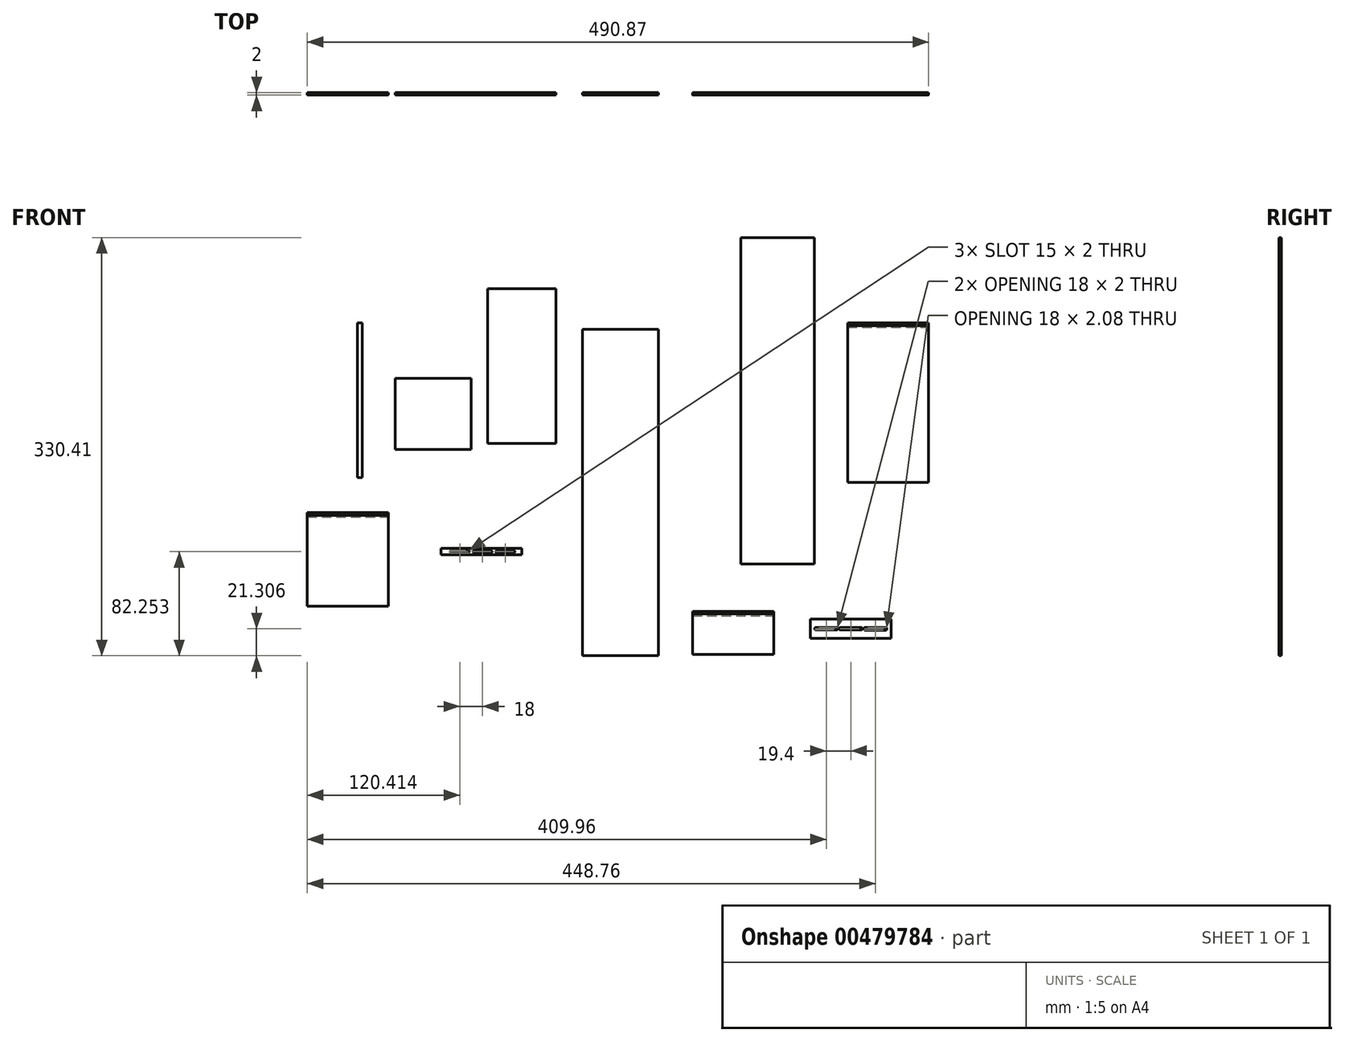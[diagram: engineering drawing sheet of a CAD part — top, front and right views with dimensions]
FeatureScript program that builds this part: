
annotation { "Feature Type Name" : "Feature", "Feature Type Description" : "" }
export const myFeature = defineFeature(function(context is Context, id is Id, definition is map)
    precondition{}
    {
        {
            var Q0;
            Q0=qCreatedBy(makeId("Front.planeOp"),FACE);
            var sketch = newSketch(context, id + "F0", { "sketchPlane" : qUnion([Q0])});
            skLineSegment(sketch, "E0.bottom", {"start": v(-75.81, 223.14) * mm, "end": v(-15.81, 223.14) * mm});
            skLineSegment(sketch, "E0.top", {"start": v(-75.81, -34.86) * mm, "end": v(-15.81, -34.86) * mm});
            skLineSegment(sketch, "E0.left", {"start": v(-75.81, 223.14) * mm, "end": v(-75.81, -34.86) * mm});
            skLineSegment(sketch, "E0.right", {"start": v(-15.81, 223.14) * mm, "end": v(-15.81, -34.86) * mm});
            skSolve(sketch);
        }
        {
            var Q0;
            Q0=makeQuery(id+"F0.imprint","IMPRINT",FACE,{"disambiguationData":[TD([[makeQuery(id+"F0.imprint","IMPRINT",EDGE,{"derivedFrom":sQuery(id+"F0.wireOp",EDGE,"E0.bottom")}),-1.0]])]});
            extrude(context, id + "F1", {"entities" : qUnion([Q0]), "depth" : 2 * mm});
        }
        {
            var Q0;
            Q0=qCreatedBy(makeId("Front.planeOp"),FACE);
            var sketch = newSketch(context, id + "F2", { "sketchPlane" : qUnion([Q0])});
            skLineSegment(sketch, "E1.bottom", {"start": v(49.18, 295.55) * mm, "end": v(107.18, 295.55) * mm});
            skLineSegment(sketch, "E1.top", {"start": v(49.18, 37.55) * mm, "end": v(107.18, 37.55) * mm});
            skLineSegment(sketch, "E1.left", {"start": v(49.18, 295.55) * mm, "end": v(49.18, 37.55) * mm});
            skLineSegment(sketch, "E1.right", {"start": v(107.18, 295.55) * mm, "end": v(107.18, 37.55) * mm});
            skSolve(sketch);
        }
        {
            var Q0;
            Q0=qSketchRegion(id+"F2",true);
            extrude(context, id + "F3", {"entities" : qUnion([Q0]), "depth" : 2 * mm});
        }
        {
            var Q0;
            Q0=qCreatedBy(makeId("Front.planeOp"),FACE);
            var sketch = newSketch(context, id + "F4", { "sketchPlane" : qUnion([Q0])});
            skLineSegment(sketch, "E2.bottom", {"start": v(-223.94, 184.27) * mm, "end": v(-163.94, 184.27) * mm});
            skLineSegment(sketch, "E2.top", {"start": v(-223.94, 128.27) * mm, "end": v(-163.94, 128.27) * mm});
            skLineSegment(sketch, "E2.left", {"start": v(-223.94, 184.27) * mm, "end": v(-223.94, 128.27) * mm});
            skLineSegment(sketch, "E2.right", {"start": v(-163.94, 184.27) * mm, "end": v(-163.94, 128.27) * mm});
            skSolve(sketch);
        }
        {
            var Q0;
            Q0=makeQuery(id+"F4.imprint","IMPRINT",FACE,{"disambiguationData":[TD([[makeQuery(id+"F4.imprint","IMPRINT",EDGE,{"derivedFrom":sQuery(id+"F4.wireOp",EDGE,"E2.bottom")}),-1.0]])]});
            extrude(context, id + "F5", {"entities" : qUnion([Q0]), "depth" : 2 * mm});
        }
        {
            var Q0;
            Q0=qCreatedBy(makeId("Front.planeOp"),FACE);
            var sketch = newSketch(context, id + "F6", { "sketchPlane" : qUnion([Q0])});
            skLineSegment(sketch, "E3.bottom", {"start": v(-187.77, 49.9) * mm, "end": v(-123.77, 49.9) * mm});
            skLineSegment(sketch, "E3.top", {"start": v(-187.77, 44.9) * mm, "end": v(-123.77, 44.9) * mm});
            skLineSegment(sketch, "E3.left", {"start": v(-187.77, 49.9) * mm, "end": v(-187.77, 44.9) * mm});
            skLineSegment(sketch, "E3.right", {"start": v(-123.77, 49.9) * mm, "end": v(-123.77, 44.9) * mm});
            skLineSegment(sketch, "E4.bottom", {"start": v(-179.36, 48.4) * mm, "end": v(-166.36, 48.4) * mm});
            skLineSegment(sketch, "E4.top", {"start": v(-179.36, 46.4) * mm, "end": v(-166.36, 46.4) * mm});
            skLineSegment(sketch, "E4.left", {"start": v(-180.36, 47.4) * mm, "end": v(-180.36, 47.4) * mm});
            skLineSegment(sketch, "E4.right", {"start": v(-165.36, 47.4) * mm, "end": v(-165.36, 47.4) * mm});
            skPoint(sketch, "E5.visualSharp", {"position": v(-180.36, 48.4) * mm});
            skArc(sketch, "E5.filletArc", {"start": v(-179.36, 48.4) * mm, "mid": v(-180.06, 48.1) * mm, "end": v(-180.36, 47.4) * mm});
            skPoint(sketch, "E6.visualSharp", {"position": v(-165.36, 48.4) * mm});
            skArc(sketch, "E6.filletArc", {"start": v(-165.36, 47.4) * mm, "mid": v(-165.65, 48.1) * mm, "end": v(-166.36, 48.4) * mm});
            skPoint(sketch, "E7.visualSharp", {"position": v(-165.36, 46.4) * mm});
            skArc(sketch, "E7.filletArc", {"start": v(-166.36, 46.4) * mm, "mid": v(-165.65, 46.69) * mm, "end": v(-165.36, 47.4) * mm});
            skPoint(sketch, "E8.visualSharp", {"position": v(-180.36, 46.4) * mm});
            skArc(sketch, "E8.filletArc", {"start": v(-180.36, 47.4) * mm, "mid": v(-180.06, 46.69) * mm, "end": v(-179.36, 46.4) * mm});
            skArc(sketch, "E9.1.0.0", {"start": v(-161.36, 48.4) * mm, "mid": v(-162.06, 48.1) * mm, "end": v(-162.36, 47.4) * mm});
            skLineSegment(sketch, "E9.1.0.1", {"start": v(-161.36, 48.4) * mm, "end": v(-148.36, 48.4) * mm});
            skArc(sketch, "E9.1.0.2", {"start": v(-147.36, 47.4) * mm, "mid": v(-147.65, 48.1) * mm, "end": v(-148.36, 48.4) * mm});
            skArc(sketch, "E9.1.0.3", {"start": v(-148.36, 46.4) * mm, "mid": v(-147.65, 46.69) * mm, "end": v(-147.36, 47.4) * mm});
            skLineSegment(sketch, "E9.1.0.4", {"start": v(-161.36, 46.4) * mm, "end": v(-148.36, 46.4) * mm});
            skArc(sketch, "E9.1.0.5", {"start": v(-162.36, 47.4) * mm, "mid": v(-162.06, 46.69) * mm, "end": v(-161.36, 46.4) * mm});
            skArc(sketch, "E9.2.0.0", {"start": v(-143.36, 48.4) * mm, "mid": v(-144.06, 48.1) * mm, "end": v(-144.36, 47.4) * mm});
            skLineSegment(sketch, "E9.2.0.1", {"start": v(-143.36, 48.4) * mm, "end": v(-130.36, 48.4) * mm});
            skArc(sketch, "E9.2.0.2", {"start": v(-129.36, 47.4) * mm, "mid": v(-129.65, 48.1) * mm, "end": v(-130.36, 48.4) * mm});
            skArc(sketch, "E9.2.0.3", {"start": v(-130.36, 46.4) * mm, "mid": v(-129.65, 46.69) * mm, "end": v(-129.36, 47.4) * mm});
            skLineSegment(sketch, "E9.2.0.4", {"start": v(-143.36, 46.4) * mm, "end": v(-130.36, 46.4) * mm});
            skArc(sketch, "E9.2.0.5", {"start": v(-144.36, 47.4) * mm, "mid": v(-144.06, 46.69) * mm, "end": v(-143.36, 46.4) * mm});
            skLineSegment(sketch, "E9.direction1", {"start": v(-180.36, 47.4) * mm, "end": v(-162.36, 47.4) * mm, "construction": true});
            skSolve(sketch);
        }
        {
            var Q0;
            Q0=qSketchRegion(id+"F6",true);
            extrude(context, id + "F7", {"entities" : qUnion([Q0]), "depth" : 2 * mm});
        }
        {
            var Q0;
            Q0=qCreatedBy(makeId("Front.planeOp"),FACE);
            var sketch = newSketch(context, id + "F8", { "sketchPlane" : qUnion([Q0])});
            skLineSegment(sketch, "E10.bottom", {"start": v(-293.27, 78.23) * mm, "end": v(-229.27, 78.23) * mm});
            skLineSegment(sketch, "E10.top", {"start": v(-293.27, 4.23) * mm, "end": v(-229.27, 4.23) * mm});
            skLineSegment(sketch, "E10.left", {"start": v(-293.27, 78.23) * mm, "end": v(-293.27, 4.23) * mm});
            skLineSegment(sketch, "E10.right", {"start": v(-229.27, 78.23) * mm, "end": v(-229.27, 4.23) * mm});
            skSolve(sketch);
        }
        {
            var Q0;
            Q0=makeQuery(id+"F8.imprint","IMPRINT",FACE,{"disambiguationData":[TD([[makeQuery(id+"F8.imprint","IMPRINT",EDGE,{"derivedFrom":sQuery(id+"F8.wireOp",EDGE,"E10.bottom")}),-1.0]])]});
            extrude(context, id + "F9", {"entities" : qUnion([Q0]), "depth" : 2 * mm});
        }
        {
            var Q0;
            Q0=qCreatedBy(makeId("Front.planeOp"),FACE);
            var sketch = newSketch(context, id + "F10", { "sketchPlane" : qUnion([Q0])});
            skLineSegment(sketch, "E11.bottom", {"start": v(104.02, -5.93) * mm, "end": v(168.02, -5.93) * mm});
            skLineSegment(sketch, "E11.top", {"start": v(104.02, -20.93) * mm, "end": v(168.02, -20.93) * mm});
            skLineSegment(sketch, "E11.left", {"start": v(104.02, -5.93) * mm, "end": v(104.02, -20.93) * mm});
            skLineSegment(sketch, "E11.right", {"start": v(168.02, -5.93) * mm, "end": v(168.02, -20.93) * mm});
            skSolve(sketch);
        }
        {
            var Q0;
            Q0=qSketchRegion(id+"F10",true);
            extrude(context, id + "F11", {"entities" : qUnion([Q0]), "depth" : 2 * mm});
        }
        {
            var Q0;
            Q0=qCreatedBy(makeId("Front.planeOp"),FACE);
            var sketch = newSketch(context, id + "F12", { "sketchPlane" : qUnion([Q0])});
            skLineSegment(sketch, "E12.bottom", {"start": v(108.46, -12.55) * mm, "end": v(124.92, -12.55) * mm});
            skLineSegment(sketch, "E12.top", {"start": v(108.46, -14.55) * mm, "end": v(124.92, -14.55) * mm});
            skLineSegment(sketch, "E12.left", {"start": v(107.69, -13.33) * mm, "end": v(107.69, -13.78) * mm});
            skLineSegment(sketch, "E12.right", {"start": v(125.69, -13.33) * mm, "end": v(125.69, -13.78) * mm});
            skLineSegment(sketch, "E13.1.0.0", {"start": v(127.86, -12.55) * mm, "end": v(144.32, -12.55) * mm});
            skLineSegment(sketch, "E13.1.0.1", {"start": v(127.86, -14.55) * mm, "end": v(144.32, -14.55) * mm});
            skLineSegment(sketch, "E13.1.0.2", {"start": v(127.09, -13.33) * mm, "end": v(127.09, -13.78) * mm});
            skLineSegment(sketch, "E13.1.0.3", {"start": v(145.09, -13.33) * mm, "end": v(145.09, -13.78) * mm});
            skLineSegment(sketch, "E13.2.0.0", {"start": v(147.26, -12.51) * mm, "end": v(163.72, -12.51) * mm});
            skLineSegment(sketch, "E13.2.0.1", {"start": v(147.26, -14.6) * mm, "end": v(163.72, -14.6) * mm});
            skLineSegment(sketch, "E13.2.0.2", {"start": v(146.49, -13.29) * mm, "end": v(146.49, -13.82) * mm});
            skLineSegment(sketch, "E13.2.0.3", {"start": v(164.49, -13.29) * mm, "end": v(164.49, -13.82) * mm});
            skLineSegment(sketch, "E13.direction1", {"start": v(107.69, -14.55) * mm, "end": v(127.09, -14.55) * mm, "construction": true});
            skPoint(sketch, "E14.visualSharp", {"position": v(107.69, -12.55) * mm});
            skArc(sketch, "E14.filletArc", {"start": v(108.46, -12.55) * mm, "mid": v(107.92, -12.78) * mm, "end": v(107.69, -13.33) * mm});
            skPoint(sketch, "E15.visualSharp", {"position": v(125.69, -12.55) * mm});
            skArc(sketch, "E15.filletArc", {"start": v(125.69, -13.33) * mm, "mid": v(125.46, -12.78) * mm, "end": v(124.92, -12.55) * mm});
            skPoint(sketch, "E16.visualSharp", {"position": v(125.69, -14.55) * mm});
            skArc(sketch, "E16.filletArc", {"start": v(124.92, -14.55) * mm, "mid": v(125.46, -14.33) * mm, "end": v(125.69, -13.78) * mm});
            skPoint(sketch, "E17.visualSharp", {"position": v(107.69, -14.55) * mm});
            skArc(sketch, "E17.filletArc", {"start": v(107.69, -13.78) * mm, "mid": v(107.92, -14.33) * mm, "end": v(108.46, -14.55) * mm});
            skPoint(sketch, "E18.visualSharp", {"position": v(127.09, -12.55) * mm});
            skArc(sketch, "E18.filletArc", {"start": v(127.86, -12.55) * mm, "mid": v(127.32, -12.78) * mm, "end": v(127.09, -13.33) * mm});
            skPoint(sketch, "E19.visualSharp", {"position": v(145.09, -12.55) * mm});
            skArc(sketch, "E19.filletArc", {"start": v(145.09, -13.33) * mm, "mid": v(144.86, -12.78) * mm, "end": v(144.32, -12.55) * mm});
            skPoint(sketch, "E20.visualSharp", {"position": v(145.09, -14.55) * mm});
            skArc(sketch, "E20.filletArc", {"start": v(144.32, -14.55) * mm, "mid": v(144.86, -14.33) * mm, "end": v(145.09, -13.78) * mm});
            skPoint(sketch, "E21.visualSharp", {"position": v(127.09, -14.55) * mm});
            skArc(sketch, "E21.filletArc", {"start": v(127.09, -13.78) * mm, "mid": v(127.32, -14.33) * mm, "end": v(127.86, -14.55) * mm});
            skPoint(sketch, "E22.visualSharp", {"position": v(146.49, -12.51) * mm});
            skArc(sketch, "E22.filletArc", {"start": v(147.26, -12.51) * mm, "mid": v(146.72, -12.74) * mm, "end": v(146.49, -13.29) * mm});
            skPoint(sketch, "E23.visualSharp", {"position": v(146.49, -14.6) * mm});
            skArc(sketch, "E23.filletArc", {"start": v(146.49, -13.82) * mm, "mid": v(146.72, -14.37) * mm, "end": v(147.26, -14.6) * mm});
            skPoint(sketch, "E24.visualSharp", {"position": v(164.49, -12.51) * mm});
            skArc(sketch, "E24.filletArc", {"start": v(164.49, -13.29) * mm, "mid": v(164.26, -12.74) * mm, "end": v(163.72, -12.51) * mm});
            skPoint(sketch, "E25.visualSharp", {"position": v(164.49, -14.6) * mm});
            skArc(sketch, "E25.filletArc", {"start": v(163.72, -14.6) * mm, "mid": v(164.26, -14.37) * mm, "end": v(164.49, -13.82) * mm});
            skSolve(sketch);
        }
        {
            var Q0;
            Q0=qSketchRegion(id+"F12",true);
            extrude(context, id + "F13", {"entities" : qUnion([Q0]), "operationType" : NewBodyOperationType.REMOVE, "depth" : 4 * mm});
        }
        {
            var Q0;
            Q0=qCreatedBy(makeId("Front.planeOp"),FACE);
            var sketch = newSketch(context, id + "F14", { "sketchPlane" : qUnion([Q0])});
            skLineSegment(sketch, "E26.bottom", {"start": v(133.6, 228.09) * mm, "end": v(197.6, 228.09) * mm});
            skLineSegment(sketch, "E26.top", {"start": v(133.6, 102.09) * mm, "end": v(197.6, 102.09) * mm});
            skLineSegment(sketch, "E26.left", {"start": v(133.6, 228.09) * mm, "end": v(133.6, 102.09) * mm});
            skLineSegment(sketch, "E26.right", {"start": v(197.6, 228.09) * mm, "end": v(197.6, 102.09) * mm});
            skSolve(sketch);
        }
        {
            var Q0;
            Q0=makeQuery(id+"F14.imprint","IMPRINT",FACE,{"disambiguationData":[TD([[makeQuery(id+"F14.imprint","IMPRINT",EDGE,{"derivedFrom":sQuery(id+"F14.wireOp",EDGE,"E26.bottom")}),-1.0]])]});
            extrude(context, id + "F15", {"entities" : qUnion([Q0]), "depth" : 2 * mm});
        }
        {
            var Q0;
            Q0=qCreatedBy(makeId("Front.planeOp"),FACE);
            var sketch = newSketch(context, id + "F16", { "sketchPlane" : qUnion([Q0])});
            skLineSegment(sketch, "E27.bottom", {"start": v(11.1, 0.17) * mm, "end": v(75.1, 0.17) * mm});
            skLineSegment(sketch, "E27.top", {"start": v(11.1, -33.83) * mm, "end": v(75.1, -33.83) * mm});
            skLineSegment(sketch, "E27.left", {"start": v(11.1, 0.17) * mm, "end": v(11.1, -33.83) * mm});
            skLineSegment(sketch, "E27.right", {"start": v(75.1, 0.17) * mm, "end": v(75.1, -33.83) * mm});
            skSolve(sketch);
        }
        {
            var Q0;
            Q0 = qSketchRegion(id + "F16", true);
            extrude(context, id + "F17", {"entities" : qUnion([Q0]), "operationType" : NewBodyOperationType.ADD, "depth" : 2 * mm});
        }
        {
            var Q0;
            Q0=qCreatedBy(makeId("Front.planeOp"),FACE);
            var sketch = newSketch(context, id + "F18", { "sketchPlane" : qUnion([Q0])});
            skLineSegment(sketch, "E28.bottom", {"start": v(-150.94, 255.06) * mm, "end": v(-96.94, 255.06) * mm});
            skLineSegment(sketch, "E28.top", {"start": v(-150.94, 133.06) * mm, "end": v(-96.94, 133.06) * mm});
            skLineSegment(sketch, "E28.left", {"start": v(-150.94, 255.06) * mm, "end": v(-150.94, 133.06) * mm});
            skLineSegment(sketch, "E28.right", {"start": v(-96.94, 255.06) * mm, "end": v(-96.94, 133.06) * mm});
            skSolve(sketch);
        }
        {
            var Q0;
            Q0 = qSketchRegion(id + "F18", true);
            extrude(context, id + "F19", {"entities" : qUnion([Q0]), "depth" : 2 * mm});
        }
        {
            var Q0;
            Q0=qCreatedBy(makeId("Front.planeOp"),FACE);
            var sketch = newSketch(context, id + "F20", { "sketchPlane" : qUnion([Q0])});
            skLineSegment(sketch, "E29.bottom", {"start": v(-253.8, 228.05) * mm, "end": v(-249.8, 228.05) * mm});
            skLineSegment(sketch, "E29.top", {"start": v(-253.8, 106.05) * mm, "end": v(-249.8, 106.05) * mm});
            skLineSegment(sketch, "E29.left", {"start": v(-253.8, 228.05) * mm, "end": v(-253.8, 106.05) * mm});
            skLineSegment(sketch, "E29.right", {"start": v(-249.8, 228.05) * mm, "end": v(-249.8, 106.05) * mm});
            skSolve(sketch);
        }
        {
            var Q0;
            Q0 = qSketchRegion(id + "F20", true);
            extrude(context, id + "F21", {"entities" : qUnion([Q0]), "depth" : 2 * mm});
        }
        {
            var Q0;
            Q0=makeQuery(id+"F9.opExtrude","SWEPT_FACE",FACE,{"disambiguationData":[OSD([sQuery(id+"F8.wireOp",EDGE,"E10.right")])]});
            var sketch = newSketch(context, id + "F22", { "sketchPlane" : qUnion([Q0])});
            skLineSegment(sketch, "E30", {"start": v(-2, 78.23) * mm, "end": v(-2, 76.23) * mm});
            skLineSegment(sketch, "E31", {"start": v(-2, 76.23) * mm, "end": v(-1.5, 76.23) * mm});
            skLineSegment(sketch, "E32", {"start": v(-1.5, 76.23) * mm, "end": v(-1.5, 75.73) * mm});
            skLineSegment(sketch, "E33", {"start": v(-0.5, 74.73) * mm, "end": v(-0.5, 74.73) * mm});
            skLineSegment(sketch, "E34", {"start": v(-0.5, 74.73) * mm, "end": v(-0.5, 78.23) * mm});
            skLineSegment(sketch, "E35", {"start": v(-0.5, 78.23) * mm, "end": v(-2, 78.23) * mm});
            skPoint(sketch, "E36.visualSharp", {"position": v(-1.5, 74.73) * mm});
            skArc(sketch, "E36.filletArc", {"start": v(-1.5, 75.73) * mm, "mid": v(-1.2, 75.02) * mm, "end": v(-0.5, 74.73) * mm});
            skSolve(sketch);
        }
        {
            var Q0;
            Q0 = qSketchRegion(id + "F22", true);
            extrude(context, id + "F23", {"entities" : qUnion([Q0]), "operationType" : NewBodyOperationType.REMOVE, "oppositeDirection" : true, "depth" : 64 * mm});
        }
        {
            var Q0;
            Q0=makeQuery(id+"F23.boolean.opBoolean","COPY",EDGE,{"derivedFrom":makeQuery(id+"F23.opExtrude","SWEPT_EDGE",EDGE,{"disambiguationData":[OSD([sQuery(id+"F8.wireOp",EDGE,"E10.bottom"),sQuery(id+"F8.wireOp",EDGE,"E10.right"),sQuery(id+"F22.wireOp",EDGE,"E34"),sQuery(id+"F22.wireOp",EDGE,"E35")])]})});
            var Q1;
            Q1=makeQuery(id+"F23.boolean.opBoolean","COPY",EDGE,{"derivedFrom":makeQuery(id+"F23.opExtrude","SWEPT_EDGE",EDGE,{"disambiguationData":[OSD([sQuery(id+"F8.wireOp",EDGE,"E10.right"),sQuery(id+"F22.wireOp",EDGE,"E30"),sQuery(id+"F22.wireOp",EDGE,"E31")])]})});
            var Q2;
            Q2=makeQuery(id+"F23.boolean.opBoolean","COPY",EDGE,{"derivedFrom":makeQuery(id+"F23.opExtrude","SWEPT_EDGE",EDGE,{"disambiguationData":[OSD([sQuery(id+"F22.wireOp",EDGE,"E31"),sQuery(id+"F22.wireOp",EDGE,"E36.filletArc")])]})});
            fillet(context, id + "F24", {"entities" : qUnion([Q0, Q1, Q2]), "radius" : 0.2 * mm, "tangentPropagation" : true, "allowEdgeOverflow" : false});
        }
        {
            var Q0;
            Q0=makeQuery(id+"F15.opExtrude","SWEPT_FACE",FACE,{"disambiguationData":[OSD([sQuery(id+"F14.wireOp",EDGE,"E26.right")])]});
            var sketch = newSketch(context, id + "F25", { "sketchPlane" : qUnion([Q0])});
            skLineSegment(sketch, "E37", {"start": v(-2, 228.09) * mm, "end": v(-2, 226.09) * mm});
            skLineSegment(sketch, "E38", {"start": v(-2, 226.09) * mm, "end": v(-1.5, 226.09) * mm});
            skLineSegment(sketch, "E39", {"start": v(-1.5, 226.09) * mm, "end": v(-1.5, 225.59) * mm});
            skLineSegment(sketch, "E40", {"start": v(-0.5, 224.59) * mm, "end": v(-0.5, 224.59) * mm});
            skLineSegment(sketch, "E41", {"start": v(-0.5, 224.59) * mm, "end": v(-0.5, 228.09) * mm});
            skLineSegment(sketch, "E42", {"start": v(-0.5, 228.09) * mm, "end": v(-2, 228.09) * mm});
            skPoint(sketch, "E43.visualSharp", {"position": v(-1.5, 224.59) * mm});
            skArc(sketch, "E43.filletArc", {"start": v(-1.5, 225.59) * mm, "mid": v(-1.2, 224.88) * mm, "end": v(-0.5, 224.59) * mm});
            skSolve(sketch);
        }
        {
            var Q0;
            Q0 = qSketchRegion(id + "F25", true);
            extrude(context, id + "F26", {"entities" : qUnion([Q0]), "operationType" : NewBodyOperationType.REMOVE, "oppositeDirection" : true, "depth" : 64 * mm});
        }
        {
            var Q0;
            Q0=makeQuery(id+"F26.boolean.opBoolean","COPY",EDGE,{"derivedFrom":makeQuery(id+"F26.opExtrude","SWEPT_EDGE",EDGE,{"disambiguationData":[OSD([sQuery(id+"F14.wireOp",EDGE,"E26.bottom"),sQuery(id+"F14.wireOp",EDGE,"E26.right"),sQuery(id+"F25.wireOp",EDGE,"E41"),sQuery(id+"F25.wireOp",EDGE,"E42")])]})});
            var Q1;
            Q1=makeQuery(id+"F26.boolean.opBoolean","COPY",EDGE,{"derivedFrom":makeQuery(id+"F26.opExtrude","SWEPT_EDGE",EDGE,{"disambiguationData":[OSD([sQuery(id+"F14.wireOp",EDGE,"E26.right"),sQuery(id+"F25.wireOp",EDGE,"E37"),sQuery(id+"F25.wireOp",EDGE,"E38")])]})});
            var Q2;
            Q2=makeQuery(id+"F26.boolean.opBoolean","COPY",EDGE,{"derivedFrom":makeQuery(id+"F26.opExtrude","SWEPT_EDGE",EDGE,{"disambiguationData":[OSD([sQuery(id+"F25.wireOp",EDGE,"E38"),sQuery(id+"F25.wireOp",EDGE,"E39")])]})});
            fillet(context, id + "F27", {"entities" : qUnion([Q0, Q1, Q2]), "radius" : 0.2 * mm, "tangentPropagation" : true, "allowEdgeOverflow" : false});
        }
        {
            var Q0;
            Q0=makeQuery(id+"F17.opExtrude","SWEPT_FACE",FACE,{"disambiguationData":[OSD([sQuery(id+"F16.wireOp",EDGE,"E27.right")])]});
            var sketch = newSketch(context, id + "F28", { "sketchPlane" : qUnion([Q0])});
            skLineSegment(sketch, "E44", {"start": v(-2, 0.17) * mm, "end": v(-2, -1.83) * mm});
            skLineSegment(sketch, "E45", {"start": v(-2, -1.83) * mm, "end": v(-1.5, -1.83) * mm});
            skLineSegment(sketch, "E46", {"start": v(-1.5, -1.83) * mm, "end": v(-1.5, -2.33) * mm});
            skLineSegment(sketch, "E47", {"start": v(-0.5, -3.33) * mm, "end": v(-0.5, -3.33) * mm});
            skLineSegment(sketch, "E48", {"start": v(-0.5, -3.33) * mm, "end": v(-0.5, 0.17) * mm});
            skLineSegment(sketch, "E49", {"start": v(-0.5, 0.17) * mm, "end": v(-2, 0.17) * mm});
            skPoint(sketch, "E50.visualSharp", {"position": v(-1.5, -3.33) * mm});
            skArc(sketch, "E50.filletArc", {"start": v(-1.5, -2.33) * mm, "mid": v(-1.2, -3.04) * mm, "end": v(-0.5, -3.33) * mm});
            skSolve(sketch);
        }
        {
            var Q0;
            Q0 = qSketchRegion(id + "F28", true);
            extrude(context, id + "F29", {"entities" : qUnion([Q0]), "operationType" : NewBodyOperationType.REMOVE, "oppositeDirection" : true, "depth" : 64 * mm});
        }
        {
            var Q0;
            Q0=makeQuery(id+"F29.boolean.opBoolean","COPY",EDGE,{"derivedFrom":makeQuery(id+"F29.opExtrude","SWEPT_EDGE",EDGE,{"disambiguationData":[OSD([sQuery(id+"F16.wireOp",EDGE,"E27.bottom"),sQuery(id+"F16.wireOp",EDGE,"E27.right"),sQuery(id+"F28.wireOp",EDGE,"E48"),sQuery(id+"F28.wireOp",EDGE,"E49")])]})});
            var Q1;
            Q1=makeQuery(id+"F29.boolean.opBoolean","COPY",EDGE,{"derivedFrom":makeQuery(id+"F29.opExtrude","SWEPT_EDGE",EDGE,{"disambiguationData":[OSD([sQuery(id+"F28.wireOp",EDGE,"E45"),sQuery(id+"F28.wireOp",EDGE,"E46")])]})});
            var Q2;
            Q2=makeQuery(id+"F29.boolean.opBoolean","COPY",EDGE,{"derivedFrom":makeQuery(id+"F29.opExtrude","SWEPT_EDGE",EDGE,{"disambiguationData":[OSD([sQuery(id+"F16.wireOp",EDGE,"E27.right"),sQuery(id+"F28.wireOp",EDGE,"E44"),sQuery(id+"F28.wireOp",EDGE,"E45")])]})});
            fillet(context, id + "F30", {"entities" : qUnion([Q0, Q1, Q2]), "radius" : 0.2 * mm, "tangentPropagation" : true, "allowEdgeOverflow" : false});
        }
    });
